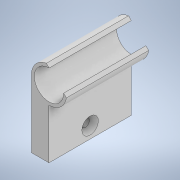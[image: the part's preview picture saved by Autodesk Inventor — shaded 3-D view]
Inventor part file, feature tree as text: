
AUTODESK INVENTOR PART (.ipt)
format: ipt  version: 2021.2 (Build 252289000, 289)  size: 205,312 bytes
history: native  units: in
note: dims shown in document units (in); Inventor stores cm internally (conversion verified against a paired STEP export)
features: sketch x4, extrude x3, hole x1
ambient origin geometry x8: Origin, YZ Plane, XZ Plane, XY Plane, X Axis, Y Axis, Z Axis, Center Point
bodies: Body1 (feature_tree)
feature tree (8):
  extrude  "Extrusion3"  Depth=0.05in
  extrude  "Extrusion4"  Depth=0.35in
  hole  "Hole1"  [1 undecoded]
  extrude  "Text"  Depth=0.2in
  sketch  "Sketch4"  dims[d10=0.5in d11=0.05in]
  sketch  "Sketch5"  dims[d12=45.0deg d13=0.35in]
  sketch  "Sketch6"  dims[d14=1.4in d15=0.0in]
  sketch  "Sketch10"  dims[d16=0.85in d17=1.4in d18=0.0in d19=0.138in d20=0.75in d21=0.28in d22=0.25in d23=0.5635in d24=0.29in d25=0.0in d28=0.045in d29=0.0in d30=0.2in d31=0.0in]
note: 1 required parameter value undecoded (feature->parameter linkage not recoverable at this tier; creation-order binding heuristic only, values carry confidence <= 0.55)
